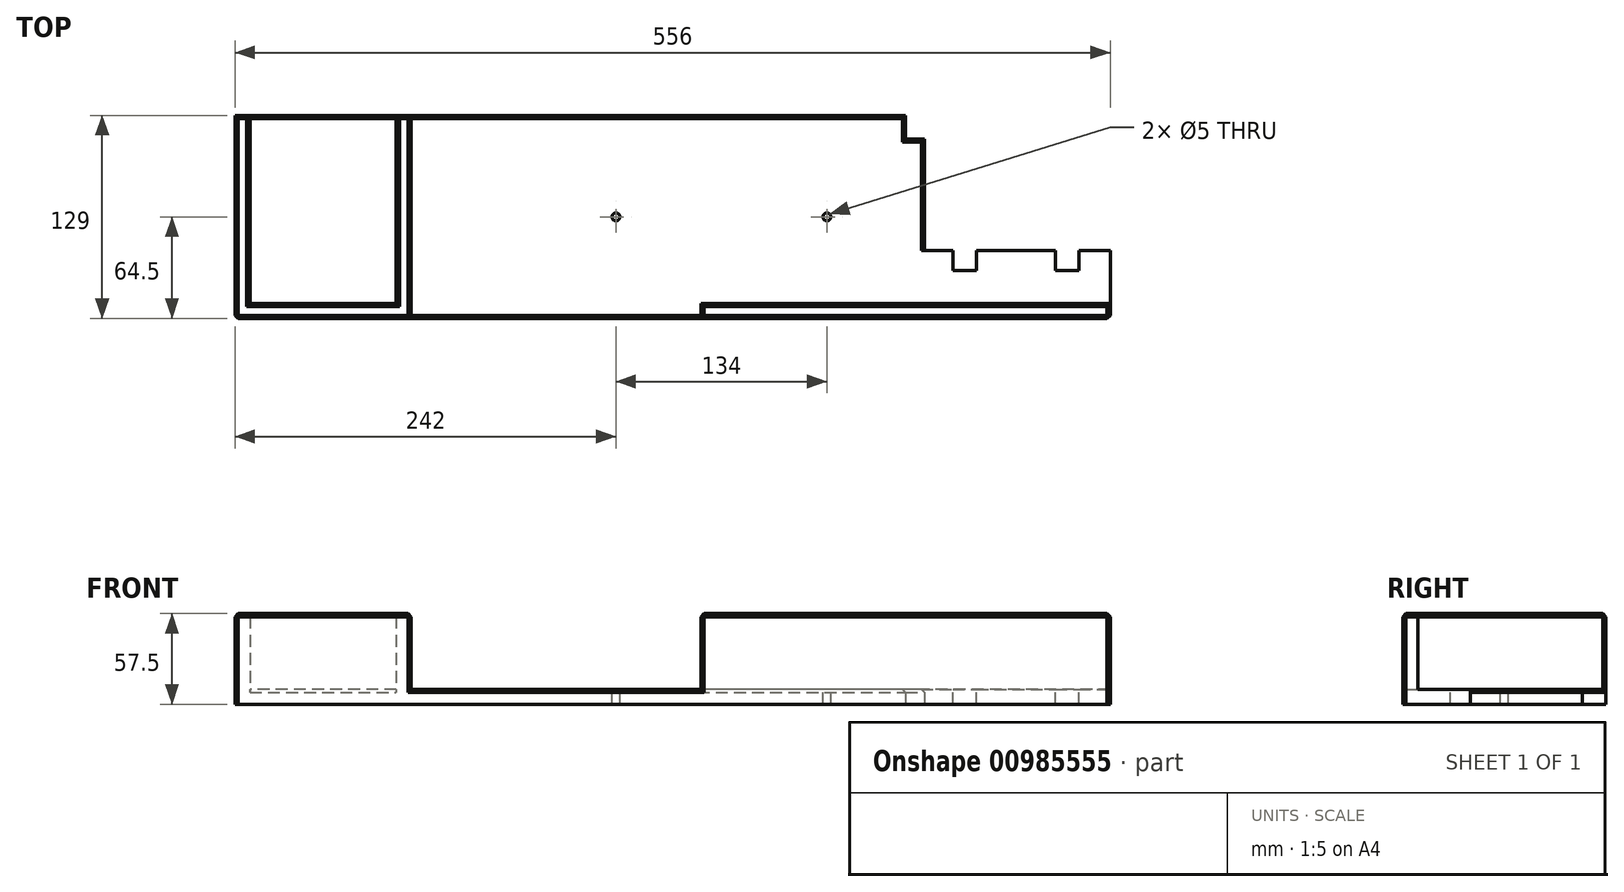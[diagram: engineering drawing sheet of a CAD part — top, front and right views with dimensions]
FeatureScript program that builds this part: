
annotation { "Feature Type Name" : "Feature", "Feature Type Description" : "" }
export const myFeature = defineFeature(function(context is Context, id is Id, definition is map)
    precondition{}
    {
        {
            var Q0;
            Q0=qCreatedBy(makeId("Top.planeOp"),FACE);
            var sketch = newSketch(context, id + "F0", { "sketchPlane" : qUnion([Q0])});
            skLineSegment(sketch, "E0", {"start": v(0, 0) * mm, "end": v(0, 129) * mm});
            skLineSegment(sketch, "E1", {"start": v(0, 129) * mm, "end": v(302.5, 129) * mm});
            skLineSegment(sketch, "E2", {"start": v(302.5, 129) * mm, "end": v(302.5, 83.1) * mm});
            skLineSegment(sketch, "E3", {"start": v(302.5, 83.1) * mm, "end": v(310, 83.1) * mm});
            skLineSegment(sketch, "E4", {"start": v(310, 83.1) * mm, "end": v(310, 33.5) * mm});
            skLineSegment(sketch, "E5", {"start": v(310, 33.5) * mm, "end": v(426, 33.5) * mm});
            skLineSegment(sketch, "E6", {"start": v(426, 33.5) * mm, "end": v(426, 114.04) * mm});
            skLineSegment(sketch, "E7", {"start": v(426, 114.04) * mm, "end": v(438, 114.04) * mm});
            skLineSegment(sketch, "E8", {"start": v(438, 114.04) * mm, "end": v(438, 43) * mm});
            skLineSegment(sketch, "E9", {"start": v(438, 43) * mm, "end": v(556, 43) * mm});
            skLineSegment(sketch, "E10", {"start": v(556, 43) * mm, "end": v(556, 0) * mm});
            skLineSegment(sketch, "E11", {"start": v(556, 0) * mm, "end": v(0, 0) * mm});
            skSolve(sketch);
        }
        {
            var Q0;
            Q0=qSketchRegion(id+"F0",true);
            extrude(context, id + "F1", {"entities" : qUnion([Q0]), "depth" : 9.5 * mm, "offsetDistance" : 25.4 * mm});
        }
        {
            var Q0;
            Q0=makeQuery(id+"F1.opExtrude","CAP_FACE",FACE,{"disambiguationData":[OSD([sQuery(id+"F0.wireOp",EDGE,"E0"),sQuery(id+"F0.wireOp",EDGE,"E1"),sQuery(id+"F0.wireOp",EDGE,"E2"),sQuery(id+"F0.wireOp",EDGE,"E3"),sQuery(id+"F0.wireOp",EDGE,"E4"),sQuery(id+"F0.wireOp",EDGE,"E5"),sQuery(id+"F0.wireOp",EDGE,"E6"),sQuery(id+"F0.wireOp",EDGE,"E7"),sQuery(id+"F0.wireOp",EDGE,"E8"),sQuery(id+"F0.wireOp",EDGE,"E9"),sQuery(id+"F0.wireOp",EDGE,"E10"),sQuery(id+"F0.wireOp",EDGE,"E11")])],"isStart":false});
            var sketch = newSketch(context, id + "F2", { "sketchPlane" : qUnion([Q0])});
            skLineSegment(sketch, "E12.bottom", {"start": v(0, 129) * mm, "end": v(9.5, 129) * mm});
            skLineSegment(sketch, "E12.top", {"start": v(0, 0) * mm, "end": v(9.5, 0) * mm});
            skLineSegment(sketch, "E12.left", {"start": v(0, 129) * mm, "end": v(0, 0) * mm});
            skLineSegment(sketch, "E12.right", {"start": v(9.5, 129) * mm, "end": v(9.5, 0) * mm});
            skLineSegment(sketch, "E13.bottom", {"start": v(0, 0) * mm, "end": v(112, 0) * mm});
            skLineSegment(sketch, "E13.top", {"start": v(0, 9.5) * mm, "end": v(112, 9.5) * mm});
            skLineSegment(sketch, "E13.left", {"start": v(0, 0) * mm, "end": v(0, 9.5) * mm});
            skLineSegment(sketch, "E13.right", {"start": v(112, 0) * mm, "end": v(112, 9.5) * mm});
            skLineSegment(sketch, "E14.bottom", {"start": v(112, 0) * mm, "end": v(102.5, 0) * mm});
            skLineSegment(sketch, "E14.top", {"start": v(112, 129) * mm, "end": v(102.5, 129) * mm});
            skLineSegment(sketch, "E14.left", {"start": v(112, 0) * mm, "end": v(112, 129) * mm});
            skLineSegment(sketch, "E14.right", {"start": v(102.5, 0) * mm, "end": v(102.5, 129) * mm});
            skSolve(sketch);
        }
        {
            var Q0;
            Q0=qSketchRegion(id+"F2",true);
            extrude(context, id + "F3", {"entities" : qUnion([Q0]), "operationType" : NewBodyOperationType.ADD, "depth" : 48 * mm, "offsetDistance" : 25.4 * mm});
        }
        {
            var Q0;
            {var subQ0=sQuery(id+"F0.wireOp",EDGE,"E10");var subQ1=sQuery(id+"F0.wireOp",EDGE,"E9");var subQ2=sQuery(id+"F0.wireOp",EDGE,"E8");var subQ3=sQuery(id+"F0.wireOp",EDGE,"E7");var subQ4=sQuery(id+"F0.wireOp",EDGE,"E6");var subQ5=sQuery(id+"F0.wireOp",EDGE,"E5");var subQ6=sQuery(id+"F0.wireOp",EDGE,"E1");var subQ7=sQuery(id+"F0.wireOp",EDGE,"E2");var subQ8=sQuery(id+"F0.wireOp",EDGE,"E3");var subQ9=sQuery(id+"F0.wireOp",EDGE,"E4");var subQ10=sQuery(id+"F0.wireOp",EDGE,"E11");Q0=makeQuery(id+"F3.boolean.opBoolean","SPLIT",FACE,{"disambiguationData":[TD([makeQuery(id+"F1.opExtrude","SWEPT_FACE",FACE,{"disambiguationData":[OSD([subQ7])]})])],"derivedFrom":makeQuery(id+"F1.opExtrude","CAP_FACE",FACE,{"disambiguationData":[OSD([sQuery(id+"F0.wireOp",EDGE,"E0"),subQ6,subQ7,subQ8,subQ9,subQ5,subQ4,subQ3,subQ2,subQ1,subQ0,subQ10])],"isStart":false})});}
            var sketch = newSketch(context, id + "F4", { "sketchPlane" : qUnion([Q0])});
            skLineSegment(sketch, "E15", {"start": v(302.5, 129) * mm, "end": v(426, 129) * mm});
            skLineSegment(sketch, "E16", {"start": v(426, 129) * mm, "end": v(426, 33.5) * mm});
            skLineSegment(sketch, "E17", {"start": v(426, 33.5) * mm, "end": v(310, 33.5) * mm});
            skLineSegment(sketch, "E18", {"start": v(310, 33.5) * mm, "end": v(310, 83.1) * mm});
            skLineSegment(sketch, "E19", {"start": v(310, 83.1) * mm, "end": v(302.5, 83.1) * mm});
            skLineSegment(sketch, "E20", {"start": v(302.5, 83.1) * mm, "end": v(302.5, 129) * mm});
            skSolve(sketch);
        }
        {
            var Q0;
            Q0 = qSketchRegion(id + "F4", true);
            extrude(context, id + "F5", {"entities" : qUnion([Q0]), "operationType" : NewBodyOperationType.ADD, "oppositeDirection" : true, "depth" : 9.5 * mm, "offsetDistance" : 25.4 * mm});
        }
        {
            var Q0;
            {var subQ0=sQuery(id+"F0.wireOp",EDGE,"E10");var subQ1=sQuery(id+"F0.wireOp",EDGE,"E9");var subQ2=sQuery(id+"F0.wireOp",EDGE,"E8");var subQ3=sQuery(id+"F0.wireOp",EDGE,"E7");var subQ4=sQuery(id+"F0.wireOp",EDGE,"E6");var subQ5=sQuery(id+"F0.wireOp",EDGE,"E5");var subQ6=sQuery(id+"F0.wireOp",EDGE,"E1");var subQ7=sQuery(id+"F0.wireOp",EDGE,"E2");var subQ8=sQuery(id+"F0.wireOp",EDGE,"E3");var subQ9=sQuery(id+"F0.wireOp",EDGE,"E4");var subQ10=sQuery(id+"F0.wireOp",EDGE,"E11");Q0=makeQuery(id+"F3.boolean.opBoolean","SPLIT",FACE,{"disambiguationData":[TD([makeQuery(id+"F1.opExtrude","SWEPT_FACE",FACE,{"disambiguationData":[OSD([subQ7])]})])],"derivedFrom":makeQuery(id+"F1.opExtrude","CAP_FACE",FACE,{"disambiguationData":[OSD([sQuery(id+"F0.wireOp",EDGE,"E0"),subQ6,subQ7,subQ8,subQ9,subQ5,subQ4,subQ3,subQ2,subQ1,subQ0,subQ10])],"isStart":false})});}
            var sketch = newSketch(context, id + "F6", { "sketchPlane" : qUnion([Q0])});
            skLineSegment(sketch, "E21", {"start": v(112, 64.5) * mm, "end": v(320.03, 64.5) * mm});
            skCircle(sketch, "E22", {"center": v(242, 64.5) * mm, "radius": 2.5 * mm});
            skCircle(sketch, "E23", {"center": v(376, 64.5) * mm, "radius": 2.5 * mm});
            skSolve(sketch);
        }
        {
            var Q0;
            {var subQ0=sQuery(id+"F6.wireOp",EDGE,"E22");var subQ1=sQuery(id+"F6.wireOp",EDGE,"E21");var subQ2=makeQuery(id+"F6.imprint","INTERSECT",VERTEX,{"disambiguationData":[OD(0.0)],"derivedFrom":[subQ1,subQ0]});Q0=makeQuery(id+"F6.imprint","IMPRINT",FACE,{"disambiguationData":[TD([[makeQuery(id+"F6.imprint","IMPRINT",EDGE,{"disambiguationData":[TD([[subQ2,-1.0]])],"derivedFrom":subQ1}),1.0]])]});}
            var Q1;
            {var subQ0=sQuery(id+"F6.wireOp",EDGE,"E22");var subQ1=sQuery(id+"F6.wireOp",EDGE,"E21");var subQ2=makeQuery(id+"F6.imprint","INTERSECT",VERTEX,{"disambiguationData":[OD(0.0)],"derivedFrom":[subQ1,subQ0]});Q1=makeQuery(id+"F6.imprint","IMPRINT",FACE,{"disambiguationData":[TD([[makeQuery(id+"F6.imprint","IMPRINT",EDGE,{"disambiguationData":[TD([[subQ2,-1.0]])],"derivedFrom":subQ1}),-1.0]])]});}
            var Q2;
            {var subQ0=sQuery(id+"F6.wireOp",EDGE,"E23");var subQ1=sQuery(id+"F6.wireOp",EDGE,"E21");var subQ2=makeQuery(id+"F6.imprint","INTERSECT",VERTEX,{"disambiguationData":[OD(0.0)],"derivedFrom":[subQ1,subQ0]});Q2=makeQuery(id+"F6.imprint","IMPRINT",FACE,{"disambiguationData":[TD([[makeQuery(id+"F6.imprint","IMPRINT",EDGE,{"disambiguationData":[TD([[subQ2,-1.0]])],"derivedFrom":subQ1}),-1.0]])]});}
            var Q3;
            {var subQ0=sQuery(id+"F6.wireOp",EDGE,"E23");var subQ1=sQuery(id+"F6.wireOp",EDGE,"E21");var subQ2=makeQuery(id+"F6.imprint","INTERSECT",VERTEX,{"disambiguationData":[OD(0.0)],"derivedFrom":[subQ1,subQ0]});Q3=makeQuery(id+"F6.imprint","IMPRINT",FACE,{"disambiguationData":[TD([[makeQuery(id+"F6.imprint","IMPRINT",EDGE,{"disambiguationData":[TD([[subQ2,-1.0]])],"derivedFrom":subQ1}),1.0]])]});}
            var Q4;
            Q4=makeQuery(id+"F6.imprint","IMPRINT",FACE,{"disambiguationData":[TD([[makeQuery(id+"F6.imprint","IMPRINT",EDGE,{"derivedFrom":sQuery(id+"F6.wireOp",EDGE,"E23")}),1.0]])]});
            var Q5;
            Q5=sQuery(id+"F6.wireOp",EDGE,"E22");
            var Q6;
            Q6=sQuery(id+"F6.wireOp",EDGE,"E23");
            extrude(context, id + "F7", {"entities" : qUnion([Q0, Q1, Q2, Q3, Q4]), "operationType" : NewBodyOperationType.REMOVE, "surfaceEntities" : qUnion([Q5, Q6]), "oppositeDirection" : true, "depth" : 25.4 * mm, "offsetDistance" : 25.4 * mm});
        }
        {
            var Q0;
            {var subQ0=sQuery(id+"F0.wireOp",EDGE,"E10");var subQ1=sQuery(id+"F0.wireOp",EDGE,"E9");var subQ2=sQuery(id+"F0.wireOp",EDGE,"E8");var subQ3=sQuery(id+"F0.wireOp",EDGE,"E7");var subQ4=sQuery(id+"F0.wireOp",EDGE,"E6");var subQ5=sQuery(id+"F0.wireOp",EDGE,"E5");var subQ6=sQuery(id+"F0.wireOp",EDGE,"E1");var subQ7=sQuery(id+"F0.wireOp",EDGE,"E2");var subQ8=sQuery(id+"F0.wireOp",EDGE,"E3");var subQ9=sQuery(id+"F0.wireOp",EDGE,"E4");var subQ10=sQuery(id+"F0.wireOp",EDGE,"E11");Q0=makeQuery(id+"F5.boolean.opBoolean","MERGE",FACE,{"derivedFrom":[makeQuery(id+"F3.boolean.opBoolean","SPLIT",FACE,{"disambiguationData":[TD([makeQuery(id+"F1.opExtrude","SWEPT_FACE",FACE,{"disambiguationData":[OSD([subQ7])]})])],"derivedFrom":makeQuery(id+"F1.opExtrude","CAP_FACE",FACE,{"disambiguationData":[OSD([sQuery(id+"F0.wireOp",EDGE,"E0"),subQ6,subQ7,subQ8,subQ9,subQ5,subQ4,subQ3,subQ2,subQ1,subQ0,subQ10])],"isStart":false})}),makeQuery(id+"F5.opExtrude","CAP_FACE",FACE,{"disambiguationData":[OSD([sQuery(id+"F4.wireOp",EDGE,"E15"),sQuery(id+"F4.wireOp",EDGE,"E16"),sQuery(id+"F4.wireOp",EDGE,"E17"),sQuery(id+"F4.wireOp",EDGE,"E18"),sQuery(id+"F4.wireOp",EDGE,"E19"),sQuery(id+"F4.wireOp",EDGE,"E20")])],"isStart":true})]});}
            var sketch = newSketch(context, id + "F8", { "sketchPlane" : qUnion([Q0])});
            skLineSegment(sketch, "E24.bottom", {"start": v(456, 43) * mm, "end": v(471, 43) * mm});
            skLineSegment(sketch, "E24.top", {"start": v(456, 30.3) * mm, "end": v(471, 30.3) * mm});
            skLineSegment(sketch, "E24.left", {"start": v(456, 43) * mm, "end": v(456, 30.3) * mm});
            skLineSegment(sketch, "E24.right", {"start": v(471, 43) * mm, "end": v(471, 30.3) * mm});
            skLineSegment(sketch, "E25.bottom", {"start": v(521, 43) * mm, "end": v(536, 43) * mm});
            skLineSegment(sketch, "E25.top", {"start": v(521, 30.3) * mm, "end": v(536, 30.3) * mm});
            skLineSegment(sketch, "E25.left", {"start": v(521, 43) * mm, "end": v(521, 30.3) * mm});
            skLineSegment(sketch, "E25.right", {"start": v(536, 43) * mm, "end": v(536, 30.3) * mm});
            skSolve(sketch);
        }
        {
            var Q0;
            Q0 = qSketchRegion(id + "F8", true);
            extrude(context, id + "F9", {"entities" : qUnion([Q0]), "operationType" : NewBodyOperationType.REMOVE, "endBound" : BoundingType.THROUGH_ALL, "oppositeDirection" : true, "depth" : 25.4 * mm, "offsetDistance" : 25.4 * mm});
        }
        {
            var Q0;
            {var subQ0=sQuery(id+"F0.wireOp",EDGE,"E10");var subQ1=sQuery(id+"F0.wireOp",EDGE,"E9");var subQ2=sQuery(id+"F0.wireOp",EDGE,"E8");var subQ3=sQuery(id+"F0.wireOp",EDGE,"E7");var subQ4=sQuery(id+"F0.wireOp",EDGE,"E6");var subQ5=sQuery(id+"F0.wireOp",EDGE,"E5");var subQ6=sQuery(id+"F0.wireOp",EDGE,"E1");var subQ7=sQuery(id+"F0.wireOp",EDGE,"E2");var subQ8=sQuery(id+"F0.wireOp",EDGE,"E3");var subQ9=sQuery(id+"F0.wireOp",EDGE,"E4");var subQ10=sQuery(id+"F0.wireOp",EDGE,"E11");Q0=makeQuery(id+"F5.boolean.opBoolean","MERGE",FACE,{"derivedFrom":[makeQuery(id+"F3.boolean.opBoolean","SPLIT",FACE,{"disambiguationData":[TD([makeQuery(id+"F1.opExtrude","SWEPT_FACE",FACE,{"disambiguationData":[OSD([subQ7])]})])],"derivedFrom":makeQuery(id+"F1.opExtrude","CAP_FACE",FACE,{"disambiguationData":[OSD([sQuery(id+"F0.wireOp",EDGE,"E0"),subQ6,subQ7,subQ8,subQ9,subQ5,subQ4,subQ3,subQ2,subQ1,subQ0,subQ10])],"isStart":false})}),makeQuery(id+"F5.opExtrude","CAP_FACE",FACE,{"disambiguationData":[OSD([sQuery(id+"F4.wireOp",EDGE,"E15"),sQuery(id+"F4.wireOp",EDGE,"E16"),sQuery(id+"F4.wireOp",EDGE,"E17"),sQuery(id+"F4.wireOp",EDGE,"E18"),sQuery(id+"F4.wireOp",EDGE,"E19"),sQuery(id+"F4.wireOp",EDGE,"E20")])],"isStart":true})]});}
            var sketch = newSketch(context, id + "F10", { "sketchPlane" : qUnion([Q0])});
            skLineSegment(sketch, "E26.bottom", {"start": v(556, 0) * mm, "end": v(295.92, 0) * mm});
            skLineSegment(sketch, "E26.top", {"start": v(556, 9.5) * mm, "end": v(295.92, 9.5) * mm});
            skLineSegment(sketch, "E26.left", {"start": v(556, 0) * mm, "end": v(556, 9.5) * mm});
            skLineSegment(sketch, "E26.right", {"start": v(295.92, 0) * mm, "end": v(295.92, 9.5) * mm});
            skSolve(sketch);
        }
        {
            var Q0;
            Q0 = qSketchRegion(id + "F10", true);
            extrude(context, id + "F11", {"entities" : qUnion([Q0]), "operationType" : NewBodyOperationType.ADD, "depth" : 48 * mm, "offsetDistance" : 25.4 * mm});
        }
        {
            var Q0;
            Q0=makeQuery(id+"F3.opExtrude","CAP_EDGE",EDGE,{"disambiguationData":[OSD([sQuery(id+"F2.wireOp",EDGE,"E12.left"),sQuery(id+"F2.wireOp",EDGE,"E13.left")])],"isStart":false});
            var Q1;
            Q1=makeQuery(id+"F3.opExtrude","CAP_EDGE",EDGE,{"disambiguationData":[OSD([sQuery(id+"F2.wireOp",EDGE,"E12.right")])],"isStart":false});
            var Q2;
            Q2=makeQuery(id+"F3.opExtrude","CAP_EDGE",EDGE,{"disambiguationData":[OSD([sQuery(id+"F2.wireOp",EDGE,"E13.bottom"),sQuery(id+"F2.wireOp",EDGE,"E14.bottom")])],"isStart":false});
            var Q3;
            Q3=makeQuery(id+"F3.opExtrude","CAP_EDGE",EDGE,{"disambiguationData":[OSD([sQuery(id+"F2.wireOp",EDGE,"E13.top")])],"isStart":false});
            var Q4;
            Q4=makeQuery(id+"F3.opExtrude","CAP_EDGE",EDGE,{"disambiguationData":[OSD([sQuery(id+"F2.wireOp",EDGE,"E14.right")])],"isStart":false});
            var Q5;
            Q5=makeQuery(id+"F3.opExtrude","CAP_EDGE",EDGE,{"disambiguationData":[OSD([sQuery(id+"F2.wireOp",EDGE,"E14.left")])],"isStart":false});
            var Q6;
            Q6=makeQuery(id+"F3.opExtrude","CAP_EDGE",EDGE,{"disambiguationData":[OSD([sQuery(id+"F2.wireOp",EDGE,"E14.top")])],"isStart":false});
            var Q7;
            Q7=makeQuery(id+"F3.opExtrude","CAP_EDGE",EDGE,{"disambiguationData":[OSD([sQuery(id+"F2.wireOp",EDGE,"E12.bottom")])],"isStart":false});
            var Q8;
            {var subQ0=sQuery(id+"F0.wireOp",EDGE,"E1");Q8=makeQuery(id+"F3.boolean.opBoolean","SPLIT",EDGE,{"disambiguationData":[TD([makeQuery(id+"F3.opExtrude","SWEPT_FACE",FACE,{"disambiguationData":[OSD([sQuery(id+"F2.wireOp",EDGE,"E12.right")])]})])],"derivedFrom":makeQuery(id+"F1.opExtrude","CAP_EDGE",EDGE,{"disambiguationData":[OSD([subQ0])],"isStart":false})});}
            var Q9;
            {var subQ0=sQuery(id+"F0.wireOp",EDGE,"E2");var subQ1=sQuery(id+"F0.wireOp",EDGE,"E1");Q9=makeQuery(id+"F5.boolean.opBoolean","MERGE",EDGE,{"derivedFrom":[makeQuery(id+"F3.boolean.opBoolean","SPLIT",EDGE,{"disambiguationData":[TD([makeQuery(id+"F1.opExtrude","SWEPT_FACE",FACE,{"disambiguationData":[OSD([subQ0])]})])],"derivedFrom":makeQuery(id+"F1.opExtrude","CAP_EDGE",EDGE,{"disambiguationData":[OSD([subQ1])],"isStart":false})}),makeQuery(id+"F5.opExtrude","CAP_EDGE",EDGE,{"disambiguationData":[OSD([sQuery(id+"F4.wireOp",EDGE,"E15")])],"isStart":true})]});}
            var Q10;
            Q10=makeQuery(id+"F1.opExtrude","CAP_EDGE",EDGE,{"disambiguationData":[OSD([sQuery(id+"F0.wireOp",EDGE,"E11")])],"isStart":false});
            var Q11;
            Q11=makeQuery(id+"F11.opExtrude","CAP_EDGE",EDGE,{"disambiguationData":[OSD([sQuery(id+"F10.wireOp",EDGE,"E26.bottom")])],"isStart":false});
            var Q12;
            Q12=makeQuery(id+"F11.opExtrude","CAP_EDGE",EDGE,{"disambiguationData":[OSD([sQuery(id+"F10.wireOp",EDGE,"E26.top")])],"isStart":false});
            var Q13;
            Q13=makeQuery(id+"F11.opExtrude","CAP_EDGE",EDGE,{"disambiguationData":[OSD([sQuery(id+"F10.wireOp",EDGE,"E26.left")])],"isStart":false});
            var Q14;
            Q14=makeQuery(id+"F1.opExtrude","CAP_EDGE",EDGE,{"disambiguationData":[OSD([sQuery(id+"F0.wireOp",EDGE,"E8")])],"isStart":false});
            var Q15;
            Q15=makeQuery(id+"F5.opExtrude","CAP_EDGE",EDGE,{"disambiguationData":[OSD([sQuery(id+"F4.wireOp",EDGE,"E16")])],"isStart":true});
            var Q16;
            Q16=makeQuery(id+"F1.opExtrude","CAP_EDGE",EDGE,{"disambiguationData":[OSD([sQuery(id+"F0.wireOp",EDGE,"E7")])],"isStart":false});
            var Q17;
            Q17=makeQuery(id+"F3.opExtrude","SWEPT_EDGE",EDGE,{"disambiguationData":[OSD([sQuery(id+"F0.wireOp",EDGE,"E11"),sQuery(id+"F2.wireOp",EDGE,"E14.bottom"),sQuery(id+"F2.wireOp",EDGE,"E14.left")])]});
            var Q18;
            Q18=makeQuery(id+"F3.boolean.opBoolean","MERGE",EDGE,{"derivedFrom":[makeQuery(id+"F1.opExtrude","SWEPT_EDGE",EDGE,{"disambiguationData":[OSD([sQuery(id+"F0.wireOp",EDGE,"E0"),sQuery(id+"F0.wireOp",EDGE,"E11")])]}),makeQuery(id+"F3.opExtrude","SWEPT_EDGE",EDGE,{"disambiguationData":[OSD([sQuery(id+"F2.wireOp",EDGE,"E13.bottom"),sQuery(id+"F2.wireOp",EDGE,"E13.left")])]})]});
            var Q19;
            Q19=makeQuery(id+"F11.opExtrude","CAP_EDGE",EDGE,{"disambiguationData":[OSD([sQuery(id+"F10.wireOp",EDGE,"E26.right")])],"isStart":false});
            var Q20;
            Q20=makeQuery(id+"F11.opExtrude","SWEPT_EDGE",EDGE,{"disambiguationData":[OSD([sQuery(id+"F0.wireOp",EDGE,"E11"),sQuery(id+"F10.wireOp",EDGE,"E26.bottom"),sQuery(id+"F10.wireOp",EDGE,"E26.right")])]});
            var Q21;
            Q21=makeQuery(id+"F11.boolean.opBoolean","MERGE",EDGE,{"derivedFrom":[makeQuery(id+"F1.opExtrude","SWEPT_EDGE",EDGE,{"disambiguationData":[OSD([sQuery(id+"F0.wireOp",EDGE,"E10"),sQuery(id+"F0.wireOp",EDGE,"E11")])]}),makeQuery(id+"F11.opExtrude","SWEPT_EDGE",EDGE,{"disambiguationData":[OSD([sQuery(id+"F10.wireOp",EDGE,"E26.bottom"),sQuery(id+"F10.wireOp",EDGE,"E26.left")])]})]});
            chamfer(context, id + "F12", {"entities" : qUnion([Q0, Q1, Q2, Q3, Q4, Q5, Q6, Q7, Q8, Q9, Q10, Q11, Q12, Q13, Q14, Q15, Q16, Q17, Q18, Q19, Q20, Q21]), "width" : 2 * mm, "tangentPropagation" : true});
        }
    });
